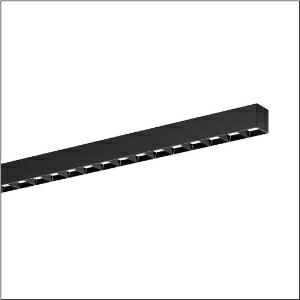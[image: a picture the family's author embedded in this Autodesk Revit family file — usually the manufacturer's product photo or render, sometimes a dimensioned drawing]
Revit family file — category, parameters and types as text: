
# Revit family: silica_r__21_51mx22tctab_4aec
name_source: partatom
category: Lighting Fixtures
units: mm (PartAtom-declared; Revit-internal decimal feet)

## family parameters
Cut with Voids When Loaded = No
Host = Face
Light Source = No
Part Type = Normal
Room Calculation Point = No
Round Connector Dimension = Use Diameter
Shared = No

## types (1)
- --- (1 x LED, 9300 lm, 80.4 W, 6500K)
    Apparent Load = 80 VA
    CIE Flux Codes = 84 100 100 100 100
    Color Rendering = 80
    Color Temperature = 6500K
    Default Elevation = 1800 mm
    Description = Silica® 21, office luminaire, primary light control with darklight reflector, of PMMA, black, CAT 2 (L<= 3000cd/m²), light emission: direct distribution, primary light characteristic: symmetric, installation type: surface-mounted, LED, rated luminous flux: 9.300lm, luminous efficacy: 110lm/W, light colour: 8tw, colour temperature: 2700..6500K, control gear: ECG DALI, with terminal, 3+2-pole, max. 2.5mm², mains connection: 220..240V, AC, 50/60Hz, rated input power: 84.5W, luminaire housing, of aluminium, jet black (RAL 9005), length: 3.004mm, width: 53mm, height: 53mm, protection rating (complete): IP20, insulation class (complete): insulation class I (protective earthing), certification: CE, permissible operating ambient temperature: 0..+35°C, standard: EN 50419, packaging unit: 1 piece
    Height = 0 mm  [stored 0 ft]
    Lamp = 1 x LED
    Lamp Light Flux = 9300 lm
    Lamp Power = 80.4 W
    Lamp count = 1
    Length = 3004 mm
    Luminous efficacy = 116 lm/W
    Manufacturer = Siteco
    ModVariant = No
    Model = 51MX22TCTAB
    Mounting Place = Ceiling
    Mounting Type = Recessed
    Number of Poles = 1
    OnlyDefault = Yes
    Power Factor = 1
    Product Name = Silica® 21
    Product group = office luminaire | ceiling recessed
    ProductGroupID = 401
    Protection Class = Protection class I
    Protection Degree = IP 20
    RLX_Detail_Level = 1
    RLX_Emergency_Light_Flux = 0 lm
    RLX_Emergency_Type = 0
    RLX_Emergency_Type_DB = No
    RlxData = <blob elided: 60713 chars, md5=d3a802b1>
    Socket = socket
    Standby Power = 0 W
    System Light Flux = 9300 lm
    System Power = 80 W
    Type Comments = individual setting
    Type Image = l_1297756.jpg
    URL = http://relux.com
    VarID = @adj_071455
    Voltage = 0 V
    Weight = 0.00 kg
    Width = 53 mm

note: [stored X ft] marks values corroborated as IEEE doubles in the binary element streams (Revit-internal decimal feet)

## geometry (parser evidence)
native form markers: Blend x4, Sweep x12
no freeform markers — native parametric forms only
